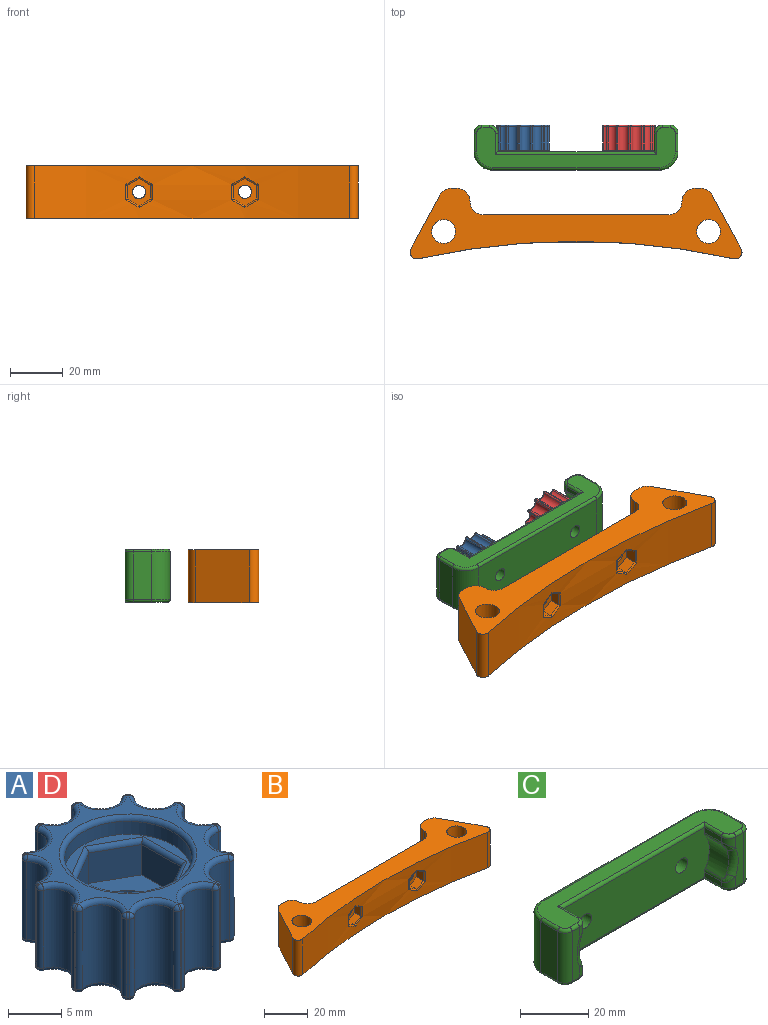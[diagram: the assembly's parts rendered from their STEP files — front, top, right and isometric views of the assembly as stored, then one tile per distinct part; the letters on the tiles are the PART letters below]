
ASSEMBLY  parts=4 mates=3
PART A: 163 faces, bbox 19.4x19.4x10 mm
  f0: cylinder r=2.5mm len=5mm, axis (0,0,-1), area 62.8mm2, adj f27,f35
  f1: plane 12x12mm, normal (0,0,1), area 26.5mm2, adj f28,f157,f158,f159,f160,f161,f162
  f2: cylinder r=10mm len=9mm, axis (0,0,-1), area 1.8mm2, adj f37,f40,f44,f45
  f3: cylinder r=2mm len=9mm, axis (0,0,-1), area 44.8mm2, adj f45,f50,f54,f55
  f4: cylinder r=10mm len=9mm, axis (0,0,-1), area 1.8mm2, adj f55,f60,f64,f65
  f5: cylinder r=2mm len=9mm, axis (0,0,-1), area 44.8mm2, adj f65,f70,f74,f75
  f6: cylinder r=10mm len=9mm, axis (0,0,-1), area 1.8mm2, adj f75,f80,f84,f85
  f7: cylinder r=2mm len=9mm, axis (0,0,-1), area 44.8mm2, adj f85,f90,f94,f95
  f8: cylinder r=10mm len=9mm, axis (0,0,-1), area 1.8mm2, adj f95,f100,f104,f105
  f9: cylinder r=2mm len=9mm, axis (0,0,-1), area 44.8mm2, adj f105,f110,f114,f115
  f10: cylinder r=10mm len=9mm, axis (0,0,-1), area 1.8mm2, adj f115,f120,f124,f125
  f11: cylinder r=2mm len=9mm, axis (0,0,-1), area 44.8mm2, adj f125,f130,f134,f135
  f12: cylinder r=10mm len=9mm, axis (0,0,-1), area 1.8mm2, adj f135,f140,f144,f145
  f13: cylinder r=2mm len=9mm, axis (0,0,-1), area 44.8mm2, adj f145,f150,f153,f156
  f14: cylinder r=10mm len=9mm, axis (0,0,-1), area 1.8mm2, adj f142,f151,f152,f156
  f15: cylinder r=2mm len=9mm, axis (0,0,-1), area 44.8mm2, adj f132,f141,f142,f143
  f16: cylinder r=10mm len=9mm, axis (0,0,-1), area 1.8mm2, adj f122,f131,f132,f133
  f17: cylinder r=2mm len=9mm, axis (0,0,-1), area 44.8mm2, adj f112,f121,f122,f123
  f18: cylinder r=10mm len=9mm, axis (0,0,-1), area 1.8mm2, adj f102,f111,f112,f113
  f19: cylinder r=2mm len=9mm, axis (0,0,-1), area 44.8mm2, adj f92,f101,f102,f103
  f20: cylinder r=10mm len=9mm, axis (0,0,-1), area 1.8mm2, adj f82,f91,f92,f93
  f21: cylinder r=2mm len=9mm, axis (0,0,-1), area 44.8mm2, adj f72,f81,f82,f83
  f22: cylinder r=10mm len=9mm, axis (0,0,-1), area 1.8mm2, adj f62,f71,f72,f73
  f23: cylinder r=2mm len=9mm, axis (0,0,-1), area 44.8mm2, adj f52,f61,f62,f63
  f24: cylinder r=10mm len=9mm, axis (0,0,-1), area 1.8mm2, adj f42,f51,f52,f53
  f25: cylinder r=2mm len=9mm, axis (0,0,-1), area 44.8mm2, adj f37,f41,f42,f43
  f26: plane 18.4x18.4mm, normal (0,0,1), area 68.7mm2, adj f36,f40,f41,f50,f51,f60,f61,f70
  f27: plane 18.4x18.4mm, normal (0,0,-1), area 181.8mm2, adj f0,f43,f44,f53,f54,f63,f64,f73
  f28: cylinder r=6mm len=12mm, axis (0,0,1), area 56.5mm2, adj f1,f36
  f29: plane 5.2x3.5mm, normal (-1,-0.01,0), area 18.2mm2, adj f30,f34,f35,f162
  f30: plane 4.53x3.5mm, normal (-0.49,-0.87,0), area 18.2mm2, adj f29,f31,f35,f160
  f31: plane 4.47x3.5mm, normal (0.51,-0.86,0), area 18.2mm2, adj f30,f32,f35,f158
  f32: plane 5.2x3.5mm, normal (1,0.01,0), area 18.2mm2, adj f31,f33,f35,f157
  f33: plane 4.53x3.5mm, normal (0.49,0.87,0), area 18.2mm2, adj f32,f34,f35,f159
  f34: plane 4.47x3.5mm, normal (-0.51,0.86,0), area 18.2mm2, adj f29,f33,f35,f161
  f35: plane 10.39x9.06mm, normal (0,0,1), area 50.5mm2, adj f0,f29,f30,f31,f32,f33,f34
  f36: torus R=6.5mm, axis (0,0,1), area 30.5mm2, adj f26,f28
  f37: cylinder r=0.5mm len=9mm, axis (0,0,1), area 6.7mm2, adj f2,f25,f38,f39
  f38: sphere r=0.5mm, area 0.4mm2, adj f37,f40,f41
  f39: sphere r=0.5mm, area 0.4mm2, adj f37,f43,f44
  f40: torus R=9.5mm, axis (0,0,1), area 0.2mm2, adj f2,f26,f38,f46
  f41: torus R=2.5mm, axis (0,0,1), area 4.3mm2, adj f25,f26,f38,f47
  f42: cylinder r=0.5mm len=9mm, axis (0,0,1), area 6.7mm2, adj f24,f25,f47,f48
  f43: torus R=2.5mm, axis (0,0,1), area 4.3mm2, adj f25,f27,f39,f48
  f44: torus R=9.5mm, axis (0,0,1), area 0.2mm2, adj f2,f27,f39,f49
  f45: cylinder r=0.5mm len=9mm, axis (0,0,1), area 6.7mm2, adj f2,f3,f46,f49
  f46: sphere r=0.5mm, area 0.4mm2, adj f40,f45,f50
  f47: sphere r=0.5mm, area 0.4mm2, adj f41,f42,f51
  f48: sphere r=0.5mm, area 0.4mm2, adj f42,f43,f53
  f49: sphere r=0.5mm, area 0.4mm2, adj f44,f45,f54
  f50: torus R=2.5mm, axis (0,0,1), area 4.3mm2, adj f3,f26,f46,f56
  f51: torus R=9.5mm, axis (0,0,1), area 0.2mm2, adj f24,f26,f47,f57
  f52: cylinder r=0.5mm len=9mm, axis (0,0,1), area 6.7mm2, adj f23,f24,f57,f58
  f53: torus R=9.5mm, axis (0,0,1), area 0.2mm2, adj f24,f27,f48,f58
  f54: torus R=2.5mm, axis (0,0,1), area 4.3mm2, adj f3,f27,f49,f59
  f55: cylinder r=0.5mm len=9mm, axis (0,0,1), area 6.7mm2, adj f3,f4,f56,f59
  f56: sphere r=0.5mm, area 0.4mm2, adj f50,f55,f60
  f57: sphere r=0.5mm, area 0.4mm2, adj f51,f52,f61
  f58: sphere r=0.5mm, area 0.4mm2, adj f52,f53,f63
  f59: sphere r=0.5mm, area 0.4mm2, adj f54,f55,f64
  f60: torus R=9.5mm, axis (0,0,1), area 0.2mm2, adj f4,f26,f56,f66
  f61: torus R=2.5mm, axis (0,0,1), area 4.3mm2, adj f23,f26,f57,f67
  f62: cylinder r=0.5mm len=9mm, axis (0,0,1), area 6.7mm2, adj f22,f23,f67,f68
  f63: torus R=2.5mm, axis (0,0,1), area 4.3mm2, adj f23,f27,f58,f68
  f64: torus R=9.5mm, axis (0,0,1), area 0.2mm2, adj f4,f27,f59,f69
  f65: cylinder r=0.5mm len=9mm, axis (0,0,1), area 6.7mm2, adj f4,f5,f66,f69
  f66: sphere r=0.5mm, area 0.4mm2, adj f60,f65,f70
  f67: sphere r=0.5mm, area 0.4mm2, adj f61,f62,f71
  f68: sphere r=0.5mm, area 0.4mm2, adj f62,f63,f73
  f69: sphere r=0.5mm, area 0.4mm2, adj f64,f65,f74
  f70: torus R=2.5mm, axis (0,0,1), area 4.3mm2, adj f5,f26,f66,f76
  f71: torus R=9.5mm, axis (0,0,1), area 0.2mm2, adj f22,f26,f67,f77
  f72: cylinder r=0.5mm len=9mm, axis (0,0,1), area 6.7mm2, adj f21,f22,f77,f78
  f73: torus R=9.5mm, axis (0,0,1), area 0.2mm2, adj f22,f27,f68,f78
  f74: torus R=2.5mm, axis (0,0,1), area 4.3mm2, adj f5,f27,f69,f79
  f75: cylinder r=0.5mm len=9mm, axis (0,0,1), area 6.7mm2, adj f5,f6,f76,f79
  f76: sphere r=0.5mm, area 0.4mm2, adj f70,f75,f80
  f77: sphere r=0.5mm, area 0.4mm2, adj f71,f72,f81
  f78: sphere r=0.5mm, area 0.4mm2, adj f72,f73,f83
  f79: sphere r=0.5mm, area 0.4mm2, adj f74,f75,f84
  f80: torus R=9.5mm, axis (0,0,1), area 0.2mm2, adj f6,f26,f76,f86
  f81: torus R=2.5mm, axis (0,0,1), area 4.3mm2, adj f21,f26,f77,f87
  f82: cylinder r=0.5mm len=9mm, axis (0,0,1), area 6.7mm2, adj f20,f21,f87,f88
  f83: torus R=2.5mm, axis (0,0,1), area 4.3mm2, adj f21,f27,f78,f88
  f84: torus R=9.5mm, axis (0,0,1), area 0.2mm2, adj f6,f27,f79,f89
  f85: cylinder r=0.5mm len=9mm, axis (0,0,1), area 6.7mm2, adj f6,f7,f86,f89
  f86: sphere r=0.5mm, area 0.4mm2, adj f80,f85,f90
  f87: sphere r=0.5mm, area 0.4mm2, adj f81,f82,f91
  f88: sphere r=0.5mm, area 0.4mm2, adj f82,f83,f93
  f89: sphere r=0.5mm, area 0.4mm2, adj f84,f85,f94
  f90: torus R=2.5mm, axis (0,0,1), area 4.3mm2, adj f7,f26,f86,f96
  f91: torus R=9.5mm, axis (0,0,1), area 0.2mm2, adj f20,f26,f87,f97
  f92: cylinder r=0.5mm len=9mm, axis (0,0,1), area 6.7mm2, adj f19,f20,f97,f98
  f93: torus R=9.5mm, axis (0,0,1), area 0.2mm2, adj f20,f27,f88,f98
  f94: torus R=2.5mm, axis (0,0,1), area 4.3mm2, adj f7,f27,f89,f99
  f95: cylinder r=0.5mm len=9mm, axis (0,0,1), area 6.7mm2, adj f7,f8,f96,f99
  f96: sphere r=0.5mm, area 0.4mm2, adj f90,f95,f100
  f97: sphere r=0.5mm, area 0.4mm2, adj f91,f92,f101
  f98: sphere r=0.5mm, area 0.4mm2, adj f92,f93,f103
  f99: sphere r=0.5mm, area 0.4mm2, adj f94,f95,f104
  f100: torus R=9.5mm, axis (0,0,1), area 0.2mm2, adj f8,f26,f96,f106
  f101: torus R=2.5mm, axis (0,0,1), area 4.3mm2, adj f19,f26,f97,f107
  f102: cylinder r=0.5mm len=9mm, axis (0,0,1), area 6.7mm2, adj f18,f19,f107,f108
  f103: torus R=2.5mm, axis (0,0,1), area 4.3mm2, adj f19,f27,f98,f108
  f104: torus R=9.5mm, axis (0,0,1), area 0.2mm2, adj f8,f27,f99,f109
  f105: cylinder r=0.5mm len=9mm, axis (0,0,1), area 6.7mm2, adj f8,f9,f106,f109
  f106: sphere r=0.5mm, area 0.4mm2, adj f100,f105,f110
  f107: sphere r=0.5mm, area 0.4mm2, adj f101,f102,f111
  f108: sphere r=0.5mm, area 0.4mm2, adj f102,f103,f113
  f109: sphere r=0.5mm, area 0.4mm2, adj f104,f105,f114
  f110: torus R=2.5mm, axis (0,0,1), area 4.3mm2, adj f9,f26,f106,f116
  f111: torus R=9.5mm, axis (0,0,1), area 0.2mm2, adj f18,f26,f107,f117
  f112: cylinder r=0.5mm len=9mm, axis (0,0,1), area 6.7mm2, adj f17,f18,f117,f118
  f113: torus R=9.5mm, axis (0,0,1), area 0.2mm2, adj f18,f27,f108,f118
  f114: torus R=2.5mm, axis (0,0,1), area 4.3mm2, adj f9,f27,f109,f119
  f115: cylinder r=0.5mm len=9mm, axis (0,0,1), area 6.7mm2, adj f9,f10,f116,f119
  f116: sphere r=0.5mm, area 0.4mm2, adj f110,f115,f120
  f117: sphere r=0.5mm, area 0.4mm2, adj f111,f112,f121
  f118: sphere r=0.5mm, area 0.4mm2, adj f112,f113,f123
  f119: sphere r=0.5mm, area 0.4mm2, adj f114,f115,f124
  f120: torus R=9.5mm, axis (0,0,1), area 0.2mm2, adj f10,f26,f116,f126
  f121: torus R=2.5mm, axis (0,0,1), area 4.3mm2, adj f17,f26,f117,f127
  f122: cylinder r=0.5mm len=9mm, axis (0,0,1), area 6.7mm2, adj f16,f17,f127,f128
  f123: torus R=2.5mm, axis (0,0,1), area 4.3mm2, adj f17,f27,f118,f128
  f124: torus R=9.5mm, axis (0,0,1), area 0.2mm2, adj f10,f27,f119,f129
  f125: cylinder r=0.5mm len=9mm, axis (0,0,1), area 6.7mm2, adj f10,f11,f126,f129
  f126: sphere r=0.5mm, area 0.4mm2, adj f120,f125,f130
  f127: sphere r=0.5mm, area 0.4mm2, adj f121,f122,f131
  f128: sphere r=0.5mm, area 0.4mm2, adj f122,f123,f133
  f129: sphere r=0.5mm, area 0.4mm2, adj f124,f125,f134
  f130: torus R=2.5mm, axis (0,0,1), area 4.3mm2, adj f11,f26,f126,f136
  f131: torus R=9.5mm, axis (0,0,1), area 0.2mm2, adj f16,f26,f127,f137
  f132: cylinder r=0.5mm len=9mm, axis (0,0,1), area 6.7mm2, adj f15,f16,f137,f138
  f133: torus R=9.5mm, axis (0,0,1), area 0.2mm2, adj f16,f27,f128,f138
  f134: torus R=2.5mm, axis (0,0,1), area 4.3mm2, adj f11,f27,f129,f139
  f135: cylinder r=0.5mm len=9mm, axis (0,0,1), area 6.7mm2, adj f11,f12,f136,f139
  f136: sphere r=0.5mm, area 0.4mm2, adj f130,f135,f140
  f137: sphere r=0.5mm, area 0.4mm2, adj f131,f132,f141
  f138: sphere r=0.5mm, area 0.4mm2, adj f132,f133,f143
  f139: sphere r=0.5mm, area 0.4mm2, adj f134,f135,f144
  f140: torus R=9.5mm, axis (0,0,1), area 0.2mm2, adj f12,f26,f136,f146
  f141: torus R=2.5mm, axis (0,0,1), area 4.3mm2, adj f15,f26,f137,f147
  f142: cylinder r=0.5mm len=9mm, axis (0,0,1), area 6.7mm2, adj f14,f15,f147,f148
  f143: torus R=2.5mm, axis (0,0,1), area 4.3mm2, adj f15,f27,f138,f148
  f144: torus R=9.5mm, axis (0,0,1), area 0.2mm2, adj f12,f27,f139,f149
  f145: cylinder r=0.5mm len=9mm, axis (0,0,1), area 6.7mm2, adj f12,f13,f146,f149
  f146: sphere r=0.5mm, area 0.4mm2, adj f140,f145,f150
  f147: sphere r=0.5mm, area 0.4mm2, adj f141,f142,f151
  f148: sphere r=0.5mm, area 0.4mm2, adj f142,f143,f152
  f149: sphere r=0.5mm, area 0.4mm2, adj f144,f145,f153
  f150: torus R=2.5mm, axis (0,0,1), area 4.3mm2, adj f13,f26,f146,f154
  f151: torus R=9.5mm, axis (0,0,1), area 0.2mm2, adj f14,f26,f147,f154
  f152: torus R=9.5mm, axis (0,0,1), area 0.2mm2, adj f14,f27,f148,f155
  f153: torus R=2.5mm, axis (0,0,1), area 4.3mm2, adj f13,f27,f149,f155
  f154: sphere r=0.5mm, area 0.4mm2, adj f150,f151,f156
  f155: sphere r=0.5mm, area 0.4mm2, adj f152,f153,f156
  f156: cylinder r=0.5mm len=9mm, axis (0,0,1), area 6.7mm2, adj f13,f14,f154,f155
  f157: cylinder r=0.5mm len=5.78mm, axis (-0.01,1,0), area 4.2mm2, adj f1,f32,f158,f159
  f158: cylinder r=0.5mm len=5.22mm, axis (0.86,0.51,0), area 4.2mm2, adj f1,f31,f157,f160
  f159: cylinder r=0.5mm len=5.28mm, axis (-0.87,0.49,0), area 4.2mm2, adj f1,f33,f157,f161
  f160: cylinder r=0.5mm len=5.28mm, axis (0.87,-0.49,0), area 4.2mm2, adj f1,f30,f158,f162
  f161: cylinder r=0.5mm len=5.22mm, axis (-0.86,-0.51,0), area 4.2mm2, adj f1,f34,f159,f162
  f162: cylinder r=0.5mm len=5.78mm, axis (0.01,-1,0), area 4.2mm2, adj f1,f29,f160,f161
PART B: 46 faces, bbox 125.3x26.6x20 mm
  f0: cylinder r=275mm len=119.25mm, axis (0,0,-1), area 2230.7mm2, adj f10,f11,f18,f19,f34,f35,f36,f37
  f1: cylinder r=2.5mm len=6mm, axis (0,1,0), area 94.2mm2, adj f8,f27
  f2: cylinder r=2.5mm len=6mm, axis (0,1,0), area 94.2mm2, adj f8,f20
  f3: plane 20x2.02mm, normal (0,1,0), area 40.3mm2, adj f10,f11,f13,f14
  f4: plane 20.29x20mm, normal (-0.88,0.47,0), area 461.1mm2, adj f10,f11,f14,f18
  f5: plane 20.29x20mm, normal (0.88,0.47,0), area 461.1mm2, adj f10,f11,f15,f19
  f6: plane 20x2.02mm, normal (0,1,0), area 40.3mm2, adj f10,f11,f15,f17
  f7: cylinder r=4.5mm len=20mm, axis (0,0,-1), area 565.5mm2, adj f10,f11
  f8: plane 70x20mm, normal (0,1,0), area 1360.7mm2, adj f1,f2,f10,f11,f12,f16
  f9: cylinder r=4.5mm len=20mm, axis (0,0,-1), area 565.5mm2, adj f10,f11
  f10: plane 125.33x26.6mm, normal (0,0,1), area 1575.4mm2, adj f0,f3,f4,f5,f6,f7,f8,f9
  f11: plane 125.33x26.6mm, normal (0,0,-1), area 1575.4mm2, adj f0,f3,f4,f5,f6,f7,f8,f9
  f12: cylinder r=5mm len=20mm, axis (0,0,1), area 157.1mm2, adj f8,f10,f11,f13
  f13: cylinder r=5mm len=20mm, axis (0,0,1), area 157.1mm2, adj f3,f10,f11,f12
  f14: cylinder r=5mm len=20mm, axis (0,0,1), area 107.6mm2, adj f3,f4,f10,f11
  f15: cylinder r=5mm len=20mm, axis (0,0,-1), area 107.6mm2, adj f5,f6,f10,f11
  f16: cylinder r=5mm len=20mm, axis (0,0,-1), area 157.1mm2, adj f8,f10,f11,f17
  f17: cylinder r=5mm len=20mm, axis (0,0,1), area 157.1mm2, adj f6,f10,f11,f16
  f18: cylinder r=2.5mm len=20mm, axis (0,0,-1), area 114.2mm2, adj f0,f4,f10,f11
  f19: cylinder r=2.5mm len=20mm, axis (0,0,-1), area 114.2mm2, adj f0,f5,f10,f11
  f20: plane 10.39x9mm, normal (0,-1,0), area 50.5mm2, adj f2,f21,f22,f23,f24,f25,f26
  f21: plane 5.2x3.91mm, normal (1,0,0), area 20.3mm2, adj f20,f22,f26,f45
  f22: plane 4.5x4.21mm, normal (0.5,0,0.87), area 21.1mm2, adj f20,f21,f23,f43,f45
  f23: plane 4.61x4.5mm, normal (-0.5,0,0.87), area 23mm2, adj f20,f22,f24,f41,f43
  f24: plane 5.2x4.64mm, normal (-1,0,0), area 24.1mm2, adj f20,f23,f25,f40,f41,f42
  f25: plane 4.61x4.5mm, normal (-0.5,0,-0.87), area 23mm2, adj f20,f24,f26,f42,f44
  f26: plane 4.5x4.21mm, normal (0.5,0,-0.87), area 21.1mm2, adj f20,f21,f25,f44,f45
  f27: plane 10.39x9mm, normal (0,-1,0), area 50.5mm2, adj f1,f28,f29,f30,f31,f32,f33
  f28: plane 5.2x3.91mm, normal (-1,0,0), area 20.3mm2, adj f27,f29,f33,f39
  f29: plane 4.5x4.21mm, normal (-0.5,0,-0.87), area 21.1mm2, adj f27,f28,f30,f37,f39
  f30: plane 4.61x4.5mm, normal (0.5,0,-0.87), area 23mm2, adj f27,f29,f31,f35,f37
  f31: plane 5.2x4.64mm, normal (1,0,0), area 24.1mm2, adj f27,f30,f32,f34,f35,f36
  f32: plane 4.61x4.5mm, normal (0.5,0,0.87), area 23mm2, adj f27,f31,f33,f36,f38
  f33: plane 4.5x4.21mm, normal (-0.5,0,0.87), area 21.1mm2, adj f27,f28,f32,f38,f39
  f34: cylinder r=0.5mm len=5.77mm, axis (0,0,-1), area 4.1mm2, adj f0,f31,f35,f36
  f35: bspline ~5.2x3.32mm, area 4.1mm2, adj f0,f30,f31,f34,f37
  f36: bspline ~5.2x3.32mm, area 4.1mm2, adj f0,f31,f32,f34,f38
  f37: bspline ~5.28x3.32mm, area 4.3mm2, adj f0,f29,f30,f35,f39
  f38: bspline ~5.28x3.32mm, area 4.3mm2, adj f0,f32,f33,f36,f39
  f39: cylinder r=0.5mm len=5.77mm, axis (0,0,-1), area 4.4mm2, adj f0,f28,f29,f33,f37,f38
  f40: cylinder r=0.5mm len=5.77mm, axis (0,0,-1), area 4.1mm2, adj f0,f24,f41,f42
  f41: bspline ~5.2x3.32mm, area 4.1mm2, adj f0,f23,f24,f40,f43
  f42: bspline ~5.2x3.32mm, area 4.1mm2, adj f0,f24,f25,f40,f44
  f43: bspline ~5.28x3.32mm, area 4.3mm2, adj f0,f22,f23,f41,f45
  f44: bspline ~5.28x3.32mm, area 4.3mm2, adj f0,f25,f26,f42,f45
  f45: cylinder r=0.5mm len=5.77mm, axis (0,0,-1), area 4.4mm2, adj f0,f21,f22,f26,f43,f44
PART C: 62 faces, bbox 78.2x18x20 mm
  f0: cylinder r=3mm len=3.9mm, axis (0,0,-1), area 12.2mm2, adj f2,f12,f33,f53
  f1: cylinder r=3mm len=3.9mm, axis (0,0,-1), area 12.2mm2, adj f15,f16,f28,f40
  f2: plane 7x1.93mm, normal (1,0,0), area 13.5mm2, adj f0,f14,f31,f55
  f3: plane 7x1.93mm, normal (-1,0,0), area 13.5mm2, adj f5,f14,f24,f59
  f4: cylinder r=3mm len=3.9mm, axis (0,0,-1), area 12.2mm2, adj f12,f13,f30,f47
  f5: cylinder r=3mm len=3.9mm, axis (0,0,-1), area 12.2mm2, adj f3,f16,f25,f61
  f6: plane 18x7mm, normal (1,0,0), area 126mm2, adj f7,f17,f34,f56
  f7: cylinder r=7mm len=18mm, axis (0,0,-1), area 197.9mm2, adj f6,f8,f35,f54
  f8: plane 63x18mm, normal (0,1,0), area 1094.7mm2, adj f7,f9,f20,f21,f37,f52
  f9: cylinder r=7mm len=18mm, axis (0,0,-1), area 197.9mm2, adj f8,f10,f39,f50
  f10: plane 18x7mm, normal (-1,0,0), area 126mm2, adj f9,f11,f41,f48
  f11: cylinder r=3mm len=18mm, axis (0,0,-1), area 84.8mm2, adj f10,f12,f43,f49
  f12: plane 18x3mm, normal (0,-1,0), area 47.1mm2, adj f0,f4,f11,f32,f45,f51
  f13: plane 7x1.93mm, normal (1,0,0), area 13.5mm2, adj f4,f14,f29,f46
  f14: plane 63x18mm, normal (0,-1,0), area 1058.1mm2, adj f2,f3,f13,f15,f20,f21,f22,f23
  f15: plane 7x1.93mm, normal (-1,0,0), area 13.5mm2, adj f1,f14,f26,f42
  f16: plane 18x3mm, normal (0,-1,0), area 47.1mm2, adj f1,f5,f17,f27,f38,f60
  f17: cylinder r=3mm len=18mm, axis (0,0,-1), area 84.8mm2, adj f6,f16,f36,f58
  f18: plane 75x15mm, normal (0,0,1), area 496.1mm2, adj f48,f49,f50,f51,f52,f53,f54,f55
  f19: plane 75x15mm, normal (0,0,-1), area 496.1mm2, adj f34,f35,f36,f37,f38,f39,f40,f41
  f20: cylinder r=2.5mm len=7mm, axis (0,-1,0), area 110mm2, adj f8,f14
  f21: cylinder r=2.5mm len=7mm, axis (0,-1,0), area 110mm2, adj f8,f14
  f22: cylinder r=11.5mm len=12.05mm, axis (0,1,0), area 100.7mm2, adj f14,f24,f25,f26,f27,f28
  f23: cylinder r=11.5mm len=12.05mm, axis (0,1,0), area 100.7mm2, adj f14,f29,f30,f31,f32,f33
  f24: cylinder r=2mm len=7mm, axis (0,1,0), area 7.7mm2, adj f3,f14,f22,f25
  f25: bspline ~3.44x3.19mm, area 7.1mm2, adj f5,f22,f24,f27
  f26: cylinder r=2mm len=7mm, axis (0,1,0), area 7.7mm2, adj f14,f15,f22,f28
  f27: torus R=13.5mm, axis (0,-1,0), area 29.8mm2, adj f16,f22,f25,f28
  f28: bspline ~3.82x3.72mm, area 7.1mm2, adj f1,f22,f26,f27
  f29: cylinder r=2mm len=7mm, axis (0,1,0), area 7.7mm2, adj f13,f14,f23,f30
  f30: bspline ~3.44x3.19mm, area 7.1mm2, adj f4,f23,f29,f32
  f31: cylinder r=2mm len=7mm, axis (0,1,0), area 7.7mm2, adj f2,f14,f23,f33
  f32: torus R=13.5mm, axis (0,1,0), area 29.8mm2, adj f12,f23,f30,f33
  f33: bspline ~3.82x3.72mm, area 7.1mm2, adj f0,f23,f31,f32
  f34: cylinder r=1mm len=7mm, axis (0,1,0), area 11mm2, adj f6,f19,f35,f36
  f35: torus R=6mm, axis (0,0,1), area 16.4mm2, adj f7,f19,f34,f37
  f36: torus R=2mm, axis (0,0,1), area 6.5mm2, adj f17,f19,f34,f38
  f37: cylinder r=1mm len=63mm, axis (-1,0,0), area 99mm2, adj f8,f19,f35,f39
  f38: cylinder r=1mm len=3mm, axis (1,0,0), area 4.7mm2, adj f16,f19,f36,f40
  f39: torus R=6mm, axis (0,0,1), area 16.4mm2, adj f9,f19,f37,f41
  f40: torus R=2mm, axis (0,0,1), area 6.5mm2, adj f1,f19,f38,f42
  f41: cylinder r=1mm len=7mm, axis (0,-1,0), area 11mm2, adj f10,f19,f39,f43
  f42: cylinder r=1mm len=8mm, axis (0,-1,0), area 11.6mm2, adj f15,f19,f40,f44
  f43: torus R=2mm, axis (0,0,1), area 6.5mm2, adj f11,f19,f41,f45
  f44: cylinder r=1mm len=61mm, axis (1,0,0), area 93.8mm2, adj f14,f19,f42,f46
  f45: cylinder r=1mm len=3mm, axis (1,0,0), area 4.7mm2, adj f12,f19,f43,f47
  f46: cylinder r=1mm len=8mm, axis (0,1,0), area 11.6mm2, adj f13,f19,f44,f47
  f47: torus R=2mm, axis (0,0,1), area 6.5mm2, adj f4,f19,f45,f46
  f48: cylinder r=1mm len=7mm, axis (0,1,0), area 11mm2, adj f10,f18,f49,f50
  f49: torus R=2mm, axis (0,0,1), area 6.5mm2, adj f11,f18,f48,f51
  f50: torus R=6mm, axis (0,0,1), area 16.4mm2, adj f9,f18,f48,f52
  f51: cylinder r=1mm len=3mm, axis (-1,0,0), area 4.7mm2, adj f12,f18,f49,f53
  f52: cylinder r=1mm len=63mm, axis (1,0,0), area 99mm2, adj f8,f18,f50,f54
  f53: torus R=2mm, axis (0,0,1), area 6.5mm2, adj f0,f18,f51,f55
  f54: torus R=6mm, axis (0,0,1), area 16.4mm2, adj f7,f18,f52,f56
  f55: cylinder r=1mm len=8mm, axis (0,-1,0), area 11.6mm2, adj f2,f18,f53,f57
  f56: cylinder r=1mm len=7mm, axis (0,-1,0), area 11mm2, adj f6,f18,f54,f58
  f57: cylinder r=1mm len=61mm, axis (-1,0,0), area 93.8mm2, adj f14,f18,f55,f59
  f58: torus R=2mm, axis (0,0,1), area 6.5mm2, adj f17,f18,f56,f60
  f59: cylinder r=1mm len=8mm, axis (0,1,0), area 11.6mm2, adj f3,f18,f57,f61
  f60: cylinder r=1mm len=3mm, axis (-1,0,0), area 4.7mm2, adj f16,f18,f58,f61
  f61: torus R=2mm, axis (0,0,1), area 6.5mm2, adj f5,f18,f59,f60
PART D: same geometry as A
PLACE A rot(axis=(-0.62,-0.55,-0.55),116.4deg) t=(-20,23.89,10.13)mm
PLACE B at identity fixed
PLACE C rot(axis=(1,0,0),180deg) t=(0,20.39,20.13)mm
PLACE D rot(axis=(-0.99,-0.1,-0.1),90.6deg) t=(20,23.89,10.13)mm
MATE slider B.f2 <-> C.f20  axis (0,1,0) through (20,0,10.13)mm
MATE revolute D.f0 <-> C.f20  axis (0,-1,0) through (20,23.89,10.13)mm
MATE revolute C.f32 <-> A.f0  axis (0,1,0) through (-20,23.89,10.13)mm
